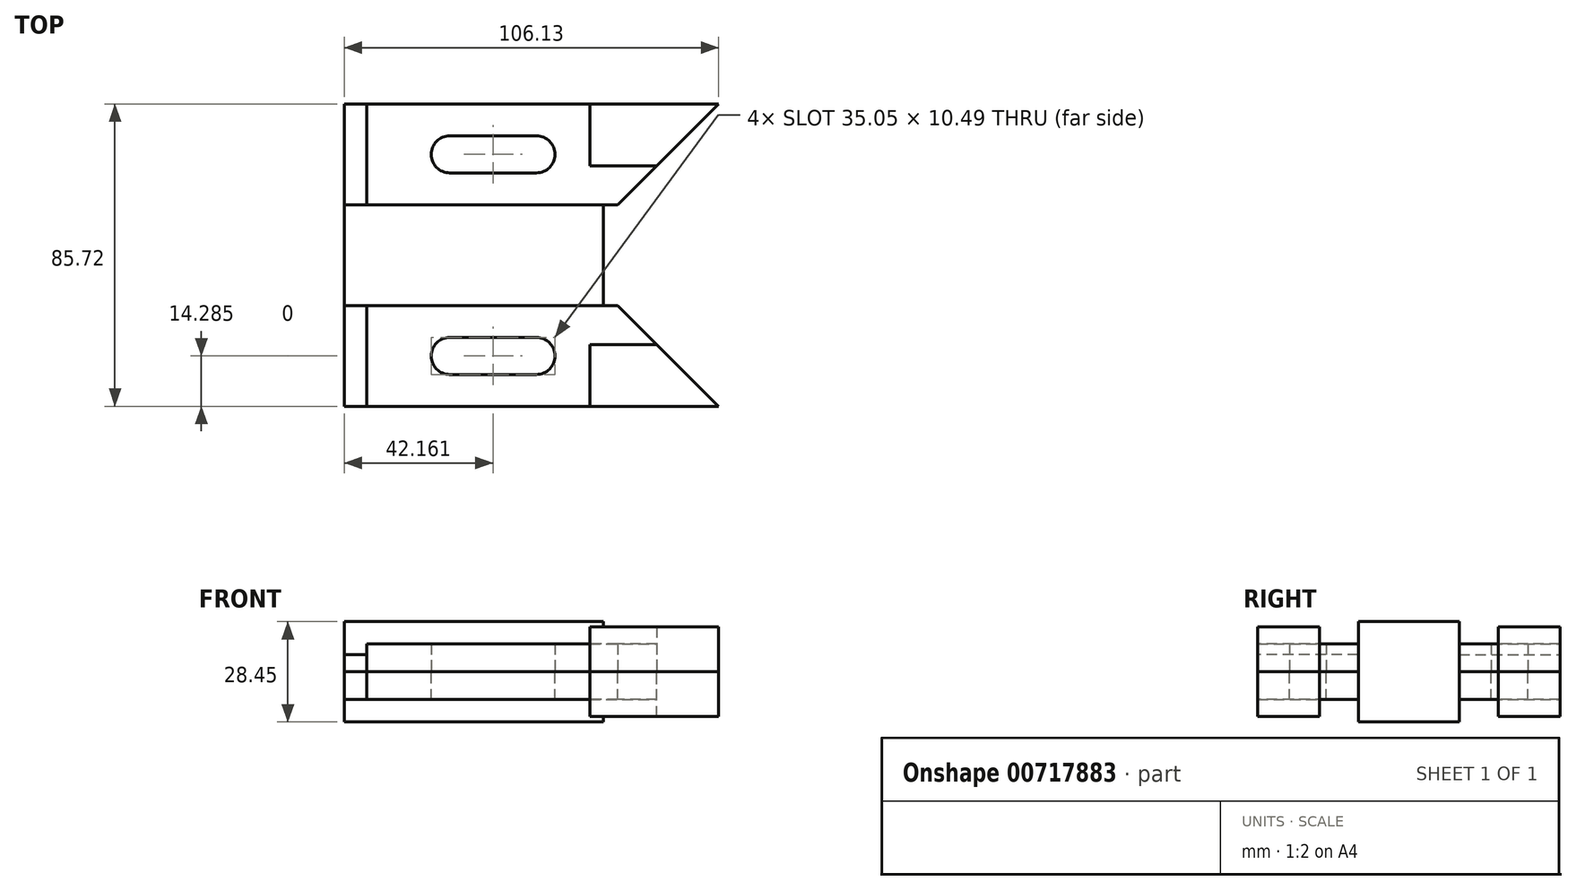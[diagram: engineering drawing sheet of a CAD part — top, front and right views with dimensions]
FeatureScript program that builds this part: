
annotation { "Feature Type Name" : "Feature", "Feature Type Description" : "" }
export const myFeature = defineFeature(function(context is Context, id is Id, definition is map)
    precondition{}
    {
        {
            var Q0;
            Q0=qCreatedBy(makeId("Top.planeOp"),FACE);
            var sketch = newSketch(context, id + "F0", { "sketchPlane" : qUnion([Q0])});
            skLineSegment(sketch, "E0.bottom", {"start": v(36.7, -14.29) * mm, "end": v(-36.7, -14.29) * mm});
            skLineSegment(sketch, "E0.top", {"start": v(36.7, 14.29) * mm, "end": v(-36.7, 14.29) * mm});
            skLineSegment(sketch, "E0.left", {"start": v(36.7, -14.29) * mm, "end": v(36.7, 14.29) * mm});
            skLineSegment(sketch, "E0.right", {"start": v(-36.7, -14.29) * mm, "end": v(-36.7, 14.29) * mm});
            skPoint(sketch, "E0.middle", {"position": v(0, 0) * mm});
            skSolve(sketch);
        }
        {
            var Q0;
            Q0=makeQuery(id+"F0.imprint","IMPRINT",FACE,{"disambiguationData":[TD([[makeQuery(id+"F0.imprint","IMPRINT",EDGE,{"derivedFrom":sQuery(id+"F0.wireOp",EDGE,"E0.bottom")}),-1.0]])]});
            extrude(context, id + "F1", {"entities" : qUnion([Q0]), "depth" : 28.45 * mm, "offsetDistance" : 25.4 * mm});
        }
        {
            var Q0;
            Q0=qCreatedBy(makeId("Top.planeOp"),FACE);
            cPlane(context, id + "F2", {"entities" : qUnion([Q0]), "cplaneType" : CPlaneType.OFFSET, "offset" : 14.22 * mm, "width" : 152.4 * mm, "height" : 152.4 * mm});
        }
        {
            var Q0;
            Q0=qCreatedBy(id+"F2.planeOp",FACE);
            var sketch = newSketch(context, id + "F3", { "sketchPlane" : qUnion([Q0])});
            skLineSegment(sketch, "E1.bottom", {"start": v(36.7, -14.29) * mm, "end": v(-36.7, -14.29) * mm});
            skLineSegment(sketch, "E1.top", {"start": v(36.7, 14.29) * mm, "end": v(-36.7, 14.29) * mm});
            skLineSegment(sketch, "E1.left", {"start": v(36.7, -14.29) * mm, "end": v(36.7, 14.29) * mm});
            skLineSegment(sketch, "E1.right", {"start": v(-36.7, -14.29) * mm, "end": v(-36.7, 14.29) * mm});
            skPoint(sketch, "E1.middle", {"position": v(0, 0) * mm});
            skLineSegment(sketch, "E2", {"start": v(-36.7, -14.29) * mm, "end": v(-36.7, -42.86) * mm});
            skLineSegment(sketch, "E3", {"start": v(-36.7, -42.86) * mm, "end": v(69.43, -42.86) * mm});
            skLineSegment(sketch, "E4", {"start": v(-30.35, -14.29) * mm, "end": v(-30.35, -42.86) * mm});
            skLineSegment(sketch, "E5", {"start": v(69.43, -42.86) * mm, "end": v(40.85, -14.29) * mm});
            skLineSegment(sketch, "E6", {"start": v(40.85, -14.29) * mm, "end": v(36.7, -14.29) * mm});
            skLineSegment(sketch, "E7", {"start": v(32.9, -42.86) * mm, "end": v(32.9, -25.34) * mm});
            skLineSegment(sketch, "E8", {"start": v(32.9, -25.34) * mm, "end": v(51.9, -25.34) * mm});
            skPoint(sketch, "E9.positionSnap0", {"position": v(-30.35, -28.58) * mm});
            skLineSegment(sketch, "E10", {"start": v(-12.07, -28.58) * mm, "end": v(22.99, -28.58) * mm, "construction": true});
            skArc(sketch, "E11", {"start": v(-12.07, -28.58) * mm, "mid": v(-10.53, -32.28) * mm, "end": v(-6.82, -33.82) * mm});
            skArc(sketch, "E12", {"start": v(-12.07, -28.58) * mm, "mid": v(-10.53, -24.87) * mm, "end": v(-6.82, -23.33) * mm});
            skArc(sketch, "E13.MirrorCS", {"start": v(22.99, -28.58) * mm, "mid": v(21.45, -24.87) * mm, "end": v(17.74, -23.33) * mm});
            skArc(sketch, "E14.MirrorCS", {"start": v(22.99, -28.58) * mm, "mid": v(21.45, -32.28) * mm, "end": v(17.74, -33.82) * mm});
            skLineSegment(sketch, "E15", {"start": v(-6.82, -23.33) * mm, "end": v(17.74, -23.33) * mm});
            skLineSegment(sketch, "E16", {"start": v(17.74, -33.82) * mm, "end": v(-6.82, -33.82) * mm});
            skLineSegment(sketch, "E17.MirrorCS", {"start": v(-36.7, 14.29) * mm, "end": v(-36.7, 42.86) * mm});
            skLineSegment(sketch, "E18.MirrorCS", {"start": v(-36.7, 42.86) * mm, "end": v(69.43, 42.86) * mm});
            skLineSegment(sketch, "E19.MirrorCS", {"start": v(-30.35, 14.29) * mm, "end": v(-30.35, 42.86) * mm});
            skLineSegment(sketch, "E20.MirrorCS", {"start": v(69.43, 42.86) * mm, "end": v(40.85, 14.29) * mm});
            skLineSegment(sketch, "E21.MirrorCS", {"start": v(40.85, 14.29) * mm, "end": v(36.7, 14.29) * mm});
            skLineSegment(sketch, "E22.MirrorCS", {"start": v(32.9, 25.34) * mm, "end": v(51.9, 25.34) * mm});
            skLineSegment(sketch, "E23.MirrorCS", {"start": v(32.9, 42.86) * mm, "end": v(32.9, 25.34) * mm});
            skLineSegment(sketch, "E24.MirrorCS", {"start": v(-6.82, 23.33) * mm, "end": v(17.74, 23.33) * mm});
            skArc(sketch, "E25.MirrorCS", {"start": v(-12.07, 28.58) * mm, "mid": v(-10.53, 24.87) * mm, "end": v(-6.82, 23.33) * mm});
            skArc(sketch, "E26.MirrorCS", {"start": v(-12.07, 28.58) * mm, "mid": v(-10.53, 32.28) * mm, "end": v(-6.82, 33.82) * mm});
            skLineSegment(sketch, "E27.MirrorCS", {"start": v(17.74, 33.82) * mm, "end": v(-6.82, 33.82) * mm});
            skArc(sketch, "E28.MirrorCS", {"start": v(22.99, 28.58) * mm, "mid": v(21.45, 32.28) * mm, "end": v(17.74, 33.82) * mm});
            skArc(sketch, "E29.MirrorCS", {"start": v(22.99, 28.58) * mm, "mid": v(21.45, 24.87) * mm, "end": v(17.74, 23.33) * mm});
            skLineSegment(sketch, "E30.MirrorCS", {"start": v(-12.07, 28.58) * mm, "end": v(22.99, 28.58) * mm, "construction": true});
            skSolve(sketch);
        }
        {
            var Q0;
            {var subQ3=sQuery(id+"F3.wireOp",EDGE,"E7");Q0=makeQuery(id+"F3.imprint","IMPRINT",FACE,{"disambiguationData":[TD([[makeQuery(id+"F3.imprint","IMPRINT",EDGE,{"derivedFrom":subQ3}),-1.0]])]});}
            var Q1;
            {var subQ4=sQuery(id+"F3.wireOp",EDGE,"E22.MirrorCS");Q1=makeQuery(id+"F3.imprint","IMPRINT",FACE,{"disambiguationData":[TD([[makeQuery(id+"F3.imprint","IMPRINT",EDGE,{"derivedFrom":subQ4}),1.0]])]});}
            extrude(context, id + "F4", {"entities" : qUnion([Q0, Q1]), "operationType" : NewBodyOperationType.ADD, "depth" : 12.7 * mm, "offsetDistance" : 25.4 * mm});
        }
        {
            var Q0;
            {var subQ4=sQuery(id+"F3.wireOp",EDGE,"E4");Q0=makeQuery(id+"F3.imprint","IMPRINT",FACE,{"disambiguationData":[TD([[makeQuery(id+"F3.imprint","IMPRINT",EDGE,{"derivedFrom":subQ4}),1.0]])]});}
            var Q1;
            {var subQ4=sQuery(id+"F3.wireOp",EDGE,"E19.MirrorCS");Q1=makeQuery(id+"F3.imprint","IMPRINT",FACE,{"disambiguationData":[TD([[makeQuery(id+"F3.imprint","IMPRINT",EDGE,{"derivedFrom":subQ4}),-1.0]])]});}
            extrude(context, id + "F5", {"entities" : qUnion([Q0, Q1]), "depth" : 7.87 * mm, "offsetDistance" : 25.4 * mm});
        }
        {
            var Q0;
            {var subQ0=sQuery(id+"F3.wireOp",EDGE,"E2");Q0=makeQuery(id+"F3.imprint","IMPRINT",FACE,{"disambiguationData":[TD([[makeQuery(id+"F3.imprint","IMPRINT",EDGE,{"derivedFrom":subQ0}),1.0]])]});}
            var Q1;
            {var subQ0=sQuery(id+"F3.wireOp",EDGE,"E17.MirrorCS");Q1=makeQuery(id+"F3.imprint","IMPRINT",FACE,{"disambiguationData":[TD([[makeQuery(id+"F3.imprint","IMPRINT",EDGE,{"derivedFrom":subQ0}),-1.0]])]});}
            extrude(context, id + "F6", {"entities" : qUnion([Q0, Q1]), "depth" : 4.83 * mm, "offsetDistance" : 25.4 * mm});
        }
        {
            var Q0;
            {var subQ0=sQuery(id+"F3.wireOp",EDGE,"E2");Q0=makeQuery(id+"F3.imprint","IMPRINT",FACE,{"disambiguationData":[TD([[makeQuery(id+"F3.imprint","IMPRINT",EDGE,{"derivedFrom":subQ0}),1.0]])]});}
            var Q1;
            {var subQ0=sQuery(id+"F3.wireOp",EDGE,"E17.MirrorCS");Q1=makeQuery(id+"F3.imprint","IMPRINT",FACE,{"disambiguationData":[TD([[makeQuery(id+"F3.imprint","IMPRINT",EDGE,{"derivedFrom":subQ0}),-1.0]])]});}
            extrude(context, id + "F7", {"entities" : qUnion([Q0, Q1]), "oppositeDirection" : true, "depth" : 7.87 * mm, "offsetDistance" : 25.4 * mm});
        }
        {
            var Q0;
            Q0=makeQuery(id+"F5.opExtrude","SWEPT_BODY",BODY,{"disambiguationData":[OSD([sQuery(id+"F3.wireOp",EDGE,"E1.top"),sQuery(id+"F3.wireOp",EDGE,"E18.MirrorCS"),sQuery(id+"F3.wireOp",EDGE,"E19.MirrorCS"),sQuery(id+"F3.wireOp",EDGE,"E20.MirrorCS"),sQuery(id+"F3.wireOp",EDGE,"E21.MirrorCS"),sQuery(id+"F3.wireOp",EDGE,"E22.MirrorCS"),sQuery(id+"F3.wireOp",EDGE,"E23.MirrorCS"),sQuery(id+"F3.wireOp",EDGE,"E24.MirrorCS"),sQuery(id+"F3.wireOp",EDGE,"E25.MirrorCS"),sQuery(id+"F3.wireOp",EDGE,"E26.MirrorCS"),sQuery(id+"F3.wireOp",EDGE,"E27.MirrorCS"),sQuery(id+"F3.wireOp",EDGE,"E28.MirrorCS"),sQuery(id+"F3.wireOp",EDGE,"E29.MirrorCS")])]});
            var Q1;
            Q1=makeQuery(id+"F4.opExtrude","SWEPT_BODY",BODY,{"disambiguationData":[OSD([sQuery(id+"F3.wireOp",EDGE,"E18.MirrorCS"),sQuery(id+"F3.wireOp",EDGE,"E20.MirrorCS"),sQuery(id+"F3.wireOp",EDGE,"E22.MirrorCS"),sQuery(id+"F3.wireOp",EDGE,"E23.MirrorCS")])]});
            var Q2;
            Q2=makeQuery(id+"F4.opExtrude","SWEPT_BODY",BODY,{"disambiguationData":[OSD([sQuery(id+"F3.wireOp",EDGE,"E3"),sQuery(id+"F3.wireOp",EDGE,"E5"),sQuery(id+"F3.wireOp",EDGE,"E7"),sQuery(id+"F3.wireOp",EDGE,"E8")])]});
            var Q3;
            Q3=makeQuery(id+"F5.opExtrude","SWEPT_BODY",BODY,{"disambiguationData":[OSD([sQuery(id+"F3.wireOp",EDGE,"E1.bottom"),sQuery(id+"F3.wireOp",EDGE,"E3"),sQuery(id+"F3.wireOp",EDGE,"E4"),sQuery(id+"F3.wireOp",EDGE,"E5"),sQuery(id+"F3.wireOp",EDGE,"E6"),sQuery(id+"F3.wireOp",EDGE,"E7"),sQuery(id+"F3.wireOp",EDGE,"E8"),sQuery(id+"F3.wireOp",EDGE,"E11"),sQuery(id+"F3.wireOp",EDGE,"E12"),sQuery(id+"F3.wireOp",EDGE,"E13.MirrorCS"),sQuery(id+"F3.wireOp",EDGE,"E14.MirrorCS"),sQuery(id+"F3.wireOp",EDGE,"E15"),sQuery(id+"F3.wireOp",EDGE,"E16")])]});
            var Q4;
            Q4=makeQuery(id+"F1.opExtrude","SWEPT_BODY",BODY,{"disambiguationData":[OSD([sQuery(id+"F0.wireOp",EDGE,"E0.bottom"),sQuery(id+"F0.wireOp",EDGE,"E0.top"),sQuery(id+"F0.wireOp",EDGE,"E0.left"),sQuery(id+"F0.wireOp",EDGE,"E0.right")])]});
            var Q5;
            Q5=qCreatedBy(id+"F2.planeOp",FACE);
            mirror(context, id + "F8", {"entities" : qUnion([Q0, Q1, Q2, Q3, Q4]), "mirrorPlane" : qUnion([Q5])});
        }
    });
